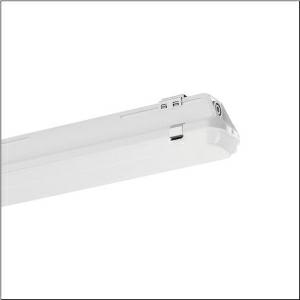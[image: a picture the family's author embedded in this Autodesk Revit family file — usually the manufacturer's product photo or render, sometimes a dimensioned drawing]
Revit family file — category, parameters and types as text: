
# Revit family: monsun_21_51fb10mp680c
name_source: partatom
category: Lighting Fixtures
units: mm (PartAtom-declared; Revit-internal decimal feet)

## family parameters
Cut with Voids When Loaded = No
Host = Face
Light Source = No
Part Type = Normal
Room Calculation Point = No
Round Connector Dimension = Use Diameter
Shared = No

## types (1)
- --- (1 x LED, 8200 lm, 46.9 W, 6500K)
    Apparent Load = 47 VA
    CIE Flux Codes = 47 77 93 94 100
    Color Rendering = 80
    Color Temperature = 6500K
    Default Elevation = 1800 mm
    Description = Monsun 21, damp-proof luminaire, chain hanger, primary optical cover: enclosure, of PMMA, light emission: direct distribution, primary light characteristic: symmetric, installation type: suspended mounting, surface-mounted, horizontal mounting, vertical mounting, LED, rated luminous flux: 8.200lm, luminous efficacy: 175lm/W, light colour: 865, colour temperature: 6500K, control gear: ON/OFF Multilumen, with terminal, 3-pole, max. 2.5mm², mains connection: 220..240V, AC, 50/60Hz, rated input power: 47W, housing, of glass-fibre reinforced polyester, uncoated, bright grey, incl. chain hanger, length: 1.590mm, width: 90mm, height: 88mm, clip for enclosure, of stainless steel (V2A), ceiling mounting element, of stainless steel (V2A), chain hanger, of stainless steel (V2A), protection rating (complete): IP66, insulation class (complete): insulation class I (protective earthing), certification: CE, ENEC, VDE, UKCA, protection symbol: D, impact resistance: IK04, permissible operating ambient temperature: -25..+35°C, standard: EN 50419, EN 60598-2-1, corresponds to IFS (International Featured Standards) requirements for safety and quality in the food industry, for indoor or canopied outdoor use, no direct snow, no direct sun, no direct rain, LABS conformity tested according to VDMA 24364:2018-05, contact your sales advisor before using the luminaires in applications with unclear chemical exposure, large temperature fluctuations or condensation-forming humidity, packaging unit: 1 piece
    Height = 89 mm
    Lamp = 1 x LED
    Lamp Light Flux = 8200 lm
    Lamp Power = 46.9 W
    Lamp count = 1
    Length = 1590 mm
    Luminous efficacy = 175 lm/W
    Manufacturer = Siteco
    ModVariant = No
    Model = 51FB10MP680C
    Mounting Place = Ceiling
    Mounting Type = Surface mounted
    Number of Poles = 1
    OnlyDefault = Yes
    Power Factor = 1
    Product Name = Monsun 21
    Product group = damp-proof luminaire
    ProductGroupID = 300
    Protection Class = Protection class I
    Protection Degree = IP 66
    RLX_Detail_Level = 1
    RLX_Emergency_Light_Flux = 0 lm
    RLX_Emergency_Type = 0
    RLX_Emergency_Type_DB = No
    RlxData = <blob elided: 89601 chars, md5=2fb4c074>
    Socket = socket
    Standby Power = 0 W
    System Light Flux = 8200 lm
    System Power = 47 W
    Type Comments = factory setting: luminous flux: 100 % | (A | C | E) | 109 mA
    Type Image = l_1319656.jpg
    URL = http://relux.com
    VarID = @adj_038381
    Voltage = 0 V
    Weight = 0.00 kg
    Width = 90 mm

## geometry (parser evidence)
native form markers: Blend x4, Sweep x14
no freeform markers — native parametric forms only
